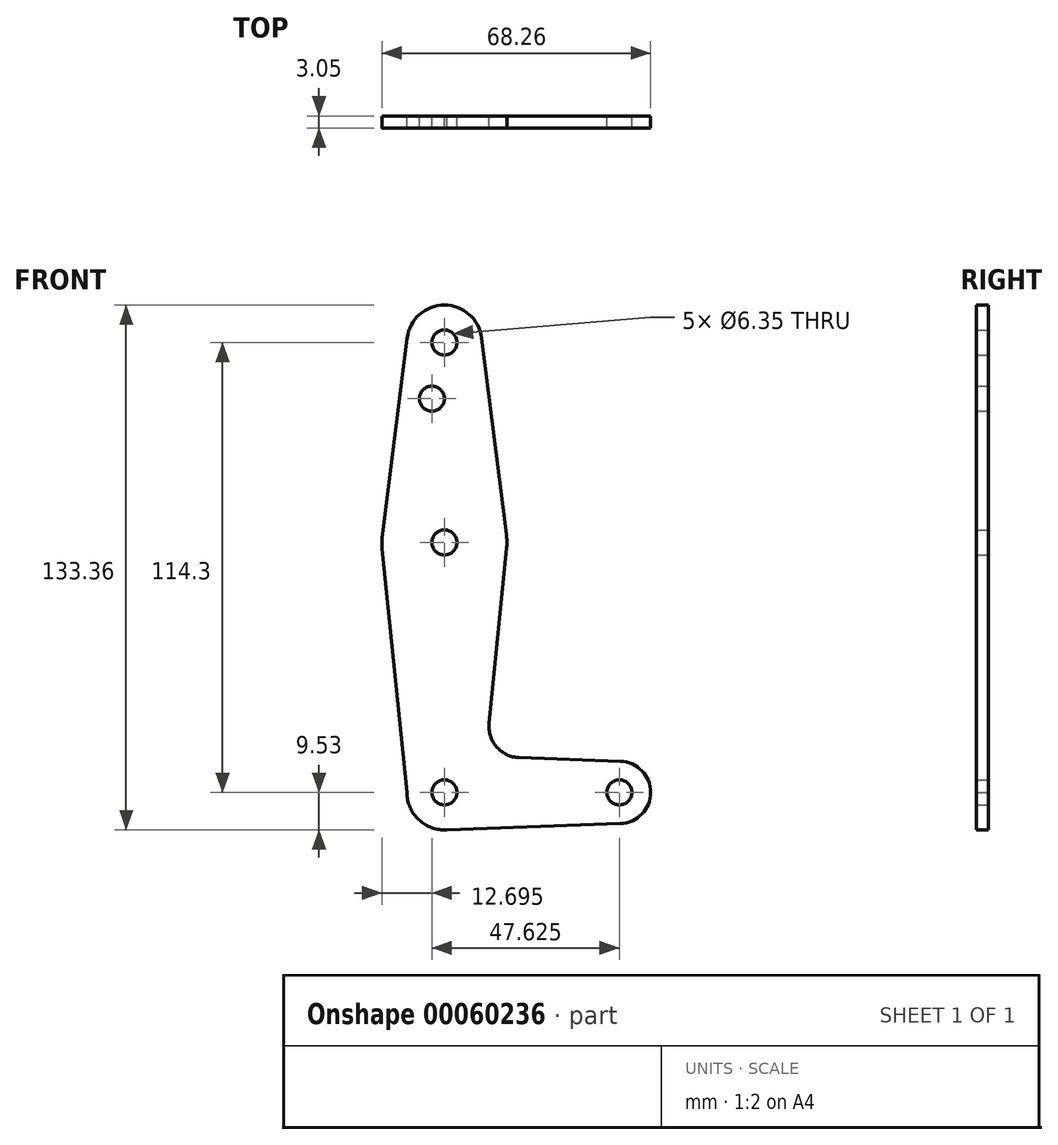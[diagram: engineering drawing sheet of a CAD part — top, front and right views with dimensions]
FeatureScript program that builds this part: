
annotation { "Feature Type Name" : "Feature", "Feature Type Description" : "" }
export const myFeature = defineFeature(function(context is Context, id is Id, definition is map)
    precondition{}
    {
        {
            var Q0;
            Q0=qCreatedBy(makeId("Front.planeOp"),FACE);
            var sketch = newSketch(context, id + "F0", { "sketchPlane" : qUnion([Q0])});
            skLineSegment(sketch, "E0", {"start": v(0, 0) * mm, "end": v(44.45, 0) * mm, "construction": true});
            skLineSegment(sketch, "E1", {"start": v(0, 0) * mm, "end": v(0, 114.3) * mm, "construction": true});
            skCircle(sketch, "E2", {"center": v(0, 114.3) * mm, "radius": 9.53 * mm});
            skCircle(sketch, "E3", {"center": v(0, 63.5) * mm, "radius": 15.88 * mm});
            skCircle(sketch, "E4", {"center": v(0, 0) * mm, "radius": 9.53 * mm});
            skCircle(sketch, "E5", {"center": v(44.45, 0) * mm, "radius": 7.94 * mm});
            skLineSegment(sketch, "E6", {"start": v(9.45, 115.5) * mm, "end": v(15.75, 65.48) * mm});
            skLineSegment(sketch, "E7", {"start": v(15.8, 61.91) * mm, "end": v(11.34, 17.59) * mm});
            skLineSegment(sketch, "E8", {"start": v(-9.53, 0) * mm, "end": v(-15.8, 61.9) * mm});
            skLineSegment(sketch, "E9", {"start": v(-15.75, 65.48) * mm, "end": v(-9.45, 115.5) * mm});
            skLineSegment(sketch, "E10", {"start": v(18.97, 8.85) * mm, "end": v(44.73, 7.93) * mm});
            skLineSegment(sketch, "E11", {"start": v(0, -9.53) * mm, "end": v(44.73, -7.93) * mm});
            skArc(sketch, "E12.filletArc", {"start": v(11.34, 17.59) * mm, "mid": v(13.26, 11.57) * mm, "end": v(18.97, 8.85) * mm});
            skCircle(sketch, "E13", {"center": v(0, 114.3) * mm, "radius": 3.18 * mm});
            skCircle(sketch, "E14", {"center": v(-3.18, 100.03) * mm, "radius": 3.18 * mm});
            skCircle(sketch, "E15", {"center": v(0, 63.5) * mm, "radius": 3.18 * mm});
            skCircle(sketch, "E16", {"center": v(0, 0) * mm, "radius": 3.18 * mm});
            skCircle(sketch, "E17", {"center": v(44.45, 0) * mm, "radius": 3.18 * mm});
            skSolve(sketch);
        }
        {
            var Q0;
            Q0 = qSketchRegion(id + "F0", true);
            extrude(context, id + "F1", {"entities" : qUnion([Q0]), "depth" : 3.05 * mm});
        }
    });
